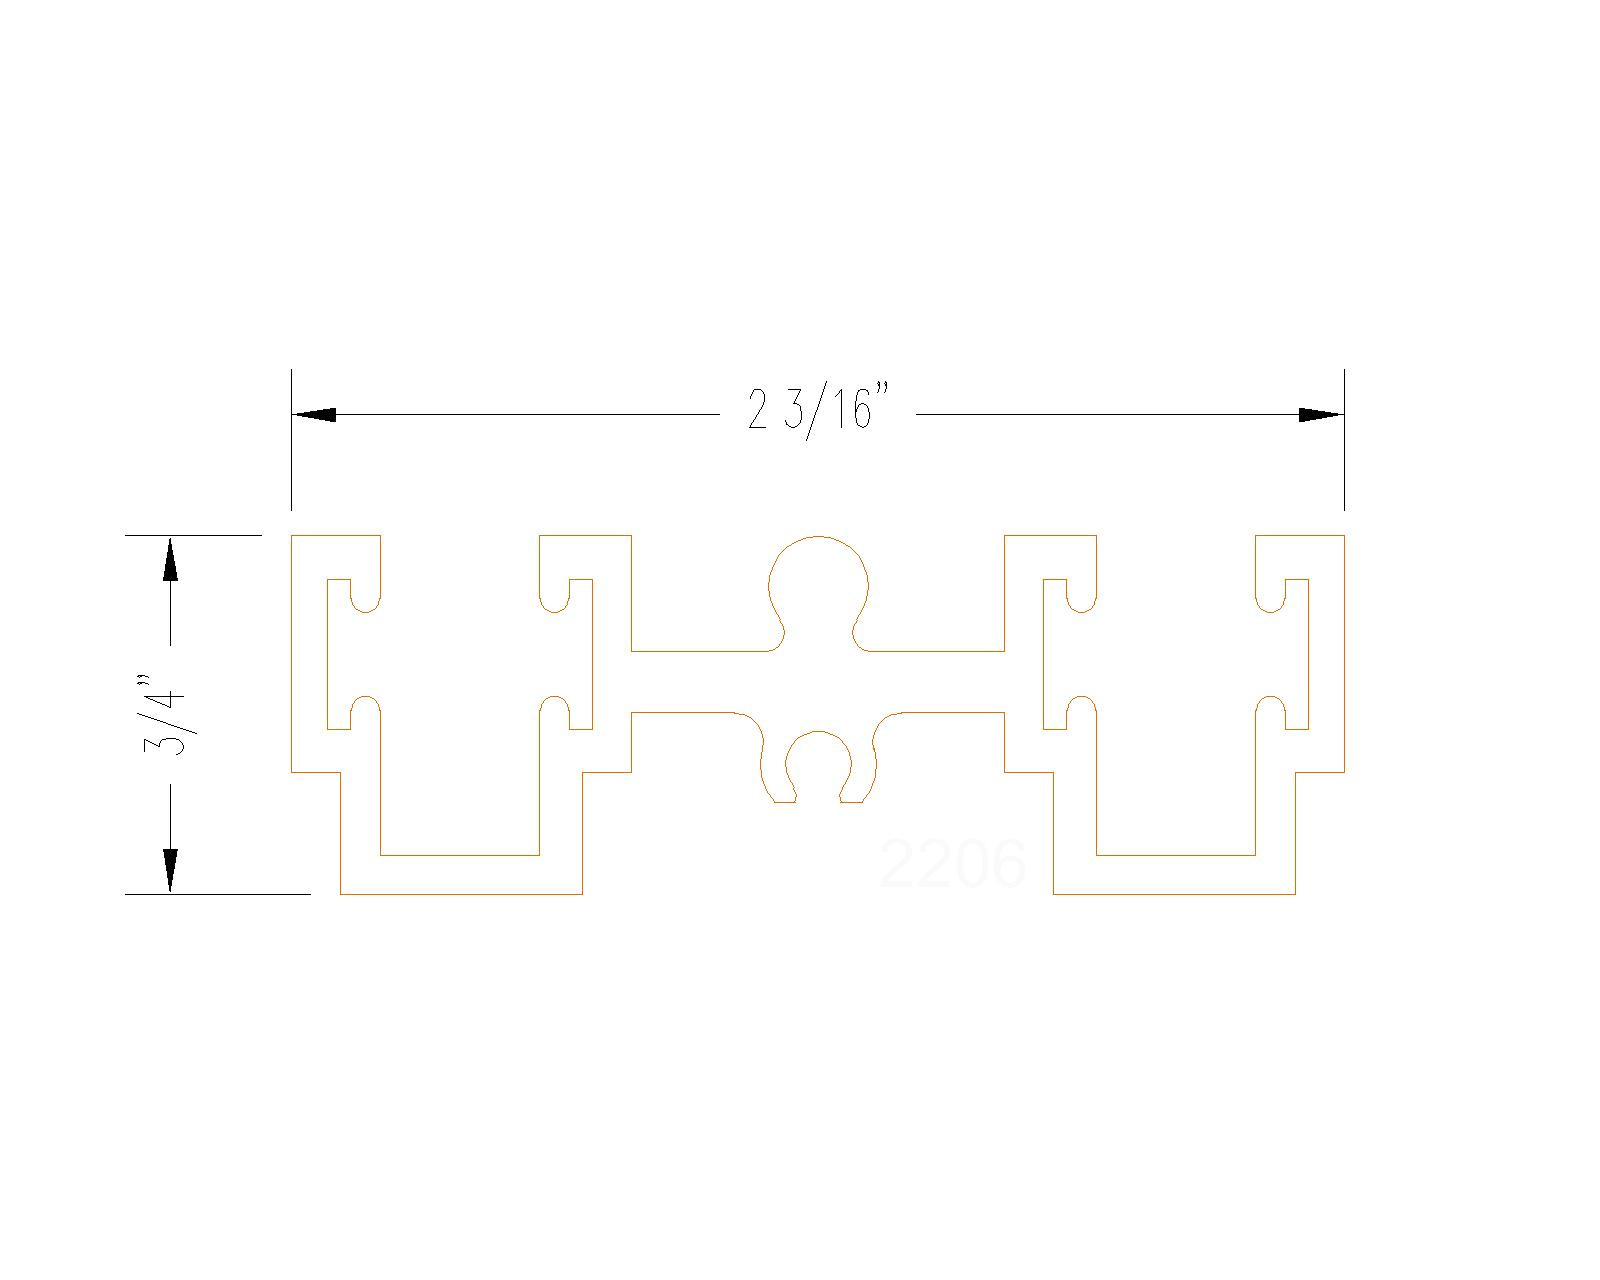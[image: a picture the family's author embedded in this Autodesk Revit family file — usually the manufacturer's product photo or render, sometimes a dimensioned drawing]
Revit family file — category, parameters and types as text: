
# Revit family: PRLMaxSlider_WallSystem
name_source: partatom
category: Puertas
units: mm (PartAtom-declared; Revit-internal decimal feet)

## family parameters
Anfitrión = Muro
Compartido = No
Corte con vacíos al cargar = No
Número OmniClass = 23.30.10.00
Punto de cálculo de habitación = No
Siempre vertical = Sí
Título OmniClass = Doors

## types (1)
- PRLMaxSlider_WallSystem
    Altura = 7' - 0"
    Altura aproximada = 7' - 0"
    Anchura = 20' - 0"
    Anchura aproximada = 20' - 0"
    Cierre de muro = Por anfitrión
    Configurations = PRL Wall System
    Fabricante = PRL
    Frame Projection Ext. = 0' - 1"
    Frame Projection Int. = 0' - 1"
    Frame Width = 0' - 3"
    Glass_Thickness = 1/2"
    H_TopRail_B = 6' - 10 11/32"
    Height = 7' - 0"
    MF2 = PRL MS
    Modelo = Max Slider MultiTrack System
    Number Fixed Panels = 1
    Number Sliding Panels = 1
    Roller Options = PRL Cancun Series (Bottom Roller)
    TH_SingleFrame = 0' - 2 3/16"
    URL = https://www.prlglass.com
    Width = 20' - 0"
    X01G = 1 1/8"
    X01W = PRL Wall System
    X02G = 1/2"
    X02M = PRL Wall System
    X03G = 1/4"
    X03P = PRL Wall System
    X04B = PRL Wall System
    XCON = PRL Wall System
    XConfig = WallSystem XO (Left) : WallSystem
    XR0 = PRL Cabo Series (Top Hung)
    XR1 = PRL Cancun Series (Bottom Roller)
    XRCON = PRL Cancun Series (Bottom Roller)
    XWSL = WallSystem XO (Left) : WallSystem
    XWSR = WallSystem OX (Right)
    formula = 0' - 1 7/16"

## geometry (parser evidence)
native form markers: Sweep x63
no freeform markers — native parametric forms only
